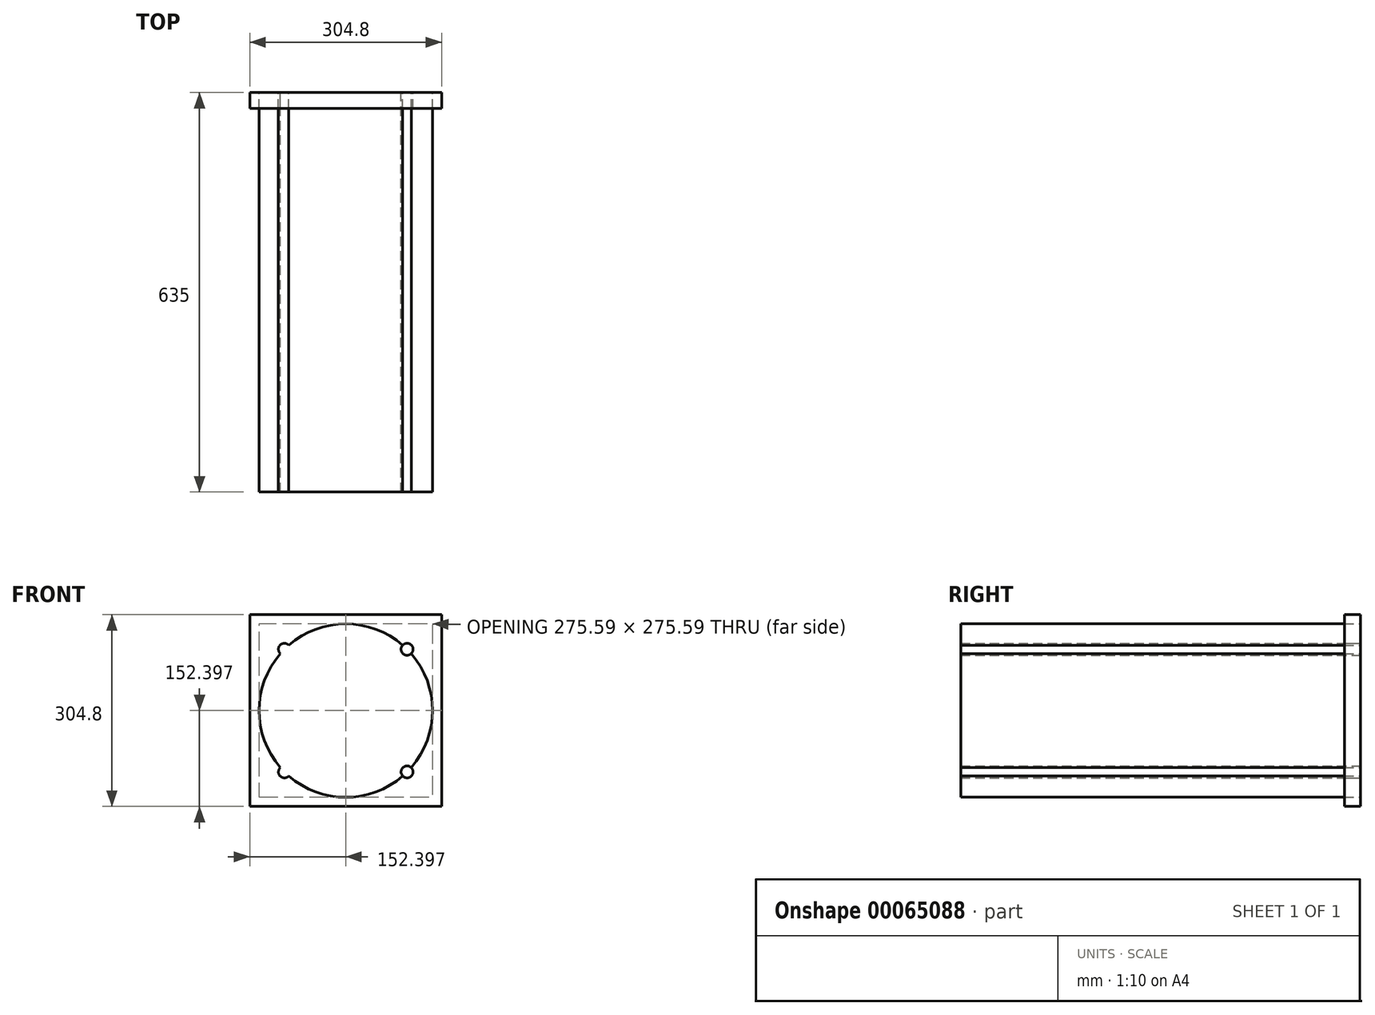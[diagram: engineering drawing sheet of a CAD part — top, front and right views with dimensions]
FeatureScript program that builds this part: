
annotation { "Feature Type Name" : "Feature", "Feature Type Description" : "" }
export const myFeature = defineFeature(function(context is Context, id is Id, definition is map)
    precondition{}
    {
        {
            var Q0;
            Q0=qCreatedBy(makeId("Front.planeOp"),FACE);
            var sketch = newSketch(context, id + "F0", { "sketchPlane" : qUnion([Q0])});
            skLineSegment(sketch, "E0.rect.bottom", {"start": v(140.94, 140.94) * mm, "end": v(-163.86, 140.94) * mm});
            skLineSegment(sketch, "E0.rect.top", {"start": v(140.94, -163.86) * mm, "end": v(-163.86, -163.86) * mm});
            skLineSegment(sketch, "E0.rect.left", {"start": v(140.94, 140.94) * mm, "end": v(140.94, -163.86) * mm});
            skLineSegment(sketch, "E0.rect.right", {"start": v(-163.86, 140.94) * mm, "end": v(-163.86, -163.86) * mm});
            skPoint(sketch, "E0.rect.middle", {"position": v(-11.46, -11.46) * mm});
            skCircle(sketch, "E1", {"center": v(-11.46, -11.46) * mm, "radius": 137.8 * mm});
            skCircle(sketch, "E2", {"center": v(-11.46, -11.46) * mm, "radius": 128.27 * mm, "construction": true});
            skLineSegment(sketch, "E3", {"start": v(-11.46, -11.46) * mm, "end": v(140.94, 140.94) * mm, "construction": true});
            skPoint(sketch, "E4", {"position": v(85.97, 85.97) * mm});
            skCircle(sketch, "E5", {"center": v(85.97, 85.97) * mm, "radius": 9.53 * mm});
            skLineSegment(sketch, "E6", {"start": v(-163.86, 140.94) * mm, "end": v(-11.46, -11.46) * mm, "construction": true});
            skCircle(sketch, "E7", {"center": v(-108.9, 85.97) * mm, "radius": 9.53 * mm});
            skLineSegment(sketch, "E8", {"start": v(-11.46, -11.46) * mm, "end": v(-163.86, -163.86) * mm, "construction": true});
            skLineSegment(sketch, "E9", {"start": v(-11.46, -11.46) * mm, "end": v(140.94, -163.86) * mm, "construction": true});
            skCircle(sketch, "E10", {"center": v(-108.9, -108.9) * mm, "radius": 9.53 * mm});
            skCircle(sketch, "E11", {"center": v(85.97, -108.9) * mm, "radius": 9.53 * mm});
            skSolve(sketch);
        }
        {
            var Q0;
            {var subQ0=sQuery(id+"F0.wireOp",EDGE,"E7");var subQ1=sQuery(id+"F0.wireOp",EDGE,"E1");var subQ2=makeQuery(id+"F0.imprint","INTERSECT",VERTEX,{"disambiguationData":[OD(0.0)],"derivedFrom":[subQ1,subQ0]});Q0=makeQuery(id+"F0.imprint","IMPRINT",FACE,{"disambiguationData":[TD([[makeQuery(id+"F0.imprint","IMPRINT",EDGE,{"disambiguationData":[TD([[subQ2,-1.0]])],"derivedFrom":subQ1}),1.0]])]});}
            var Q1;
            {var subQ0=sQuery(id+"F0.wireOp",EDGE,"E7");var subQ1=sQuery(id+"F0.wireOp",EDGE,"E1");var subQ2=makeQuery(id+"F0.imprint","INTERSECT",VERTEX,{"disambiguationData":[OD(0.0)],"derivedFrom":[subQ1,subQ0]});Q1=makeQuery(id+"F0.imprint","IMPRINT",FACE,{"disambiguationData":[TD([[makeQuery(id+"F0.imprint","IMPRINT",EDGE,{"disambiguationData":[TD([[subQ2,-1.0]])],"derivedFrom":subQ1}),-1.0]])]});}
            var Q2;
            {var subQ0=sQuery(id+"F0.wireOp",EDGE,"E5");var subQ1=sQuery(id+"F0.wireOp",EDGE,"E1");var subQ2=makeQuery(id+"F0.imprint","INTERSECT",VERTEX,{"disambiguationData":[OD(0.0)],"derivedFrom":[subQ1,subQ0]});Q2=makeQuery(id+"F0.imprint","IMPRINT",FACE,{"disambiguationData":[TD([[makeQuery(id+"F0.imprint","IMPRINT",EDGE,{"disambiguationData":[TD([[subQ2,1.0]])],"derivedFrom":subQ1}),-1.0]])]});}
            var Q3;
            {var subQ0=sQuery(id+"F0.wireOp",EDGE,"E5");var subQ1=sQuery(id+"F0.wireOp",EDGE,"E1");var subQ2=makeQuery(id+"F0.imprint","INTERSECT",VERTEX,{"disambiguationData":[OD(0.0)],"derivedFrom":[subQ1,subQ0]});Q3=makeQuery(id+"F0.imprint","IMPRINT",FACE,{"disambiguationData":[TD([[makeQuery(id+"F0.imprint","IMPRINT",EDGE,{"disambiguationData":[TD([[subQ2,1.0]])],"derivedFrom":subQ1}),1.0]])]});}
            var Q4;
            {var subQ0=sQuery(id+"F0.wireOp",EDGE,"E10");var subQ1=sQuery(id+"F0.wireOp",EDGE,"E1");var subQ2=makeQuery(id+"F0.imprint","INTERSECT",VERTEX,{"disambiguationData":[OD(0.0)],"derivedFrom":[subQ1,subQ0]});Q4=makeQuery(id+"F0.imprint","IMPRINT",FACE,{"disambiguationData":[TD([[makeQuery(id+"F0.imprint","IMPRINT",EDGE,{"disambiguationData":[TD([[subQ2,-1.0]])],"derivedFrom":subQ1}),-1.0]])]});}
            var Q5;
            {var subQ0=sQuery(id+"F0.wireOp",EDGE,"E10");var subQ1=sQuery(id+"F0.wireOp",EDGE,"E1");var subQ2=makeQuery(id+"F0.imprint","INTERSECT",VERTEX,{"disambiguationData":[OD(0.0)],"derivedFrom":[subQ1,subQ0]});Q5=makeQuery(id+"F0.imprint","IMPRINT",FACE,{"disambiguationData":[TD([[makeQuery(id+"F0.imprint","IMPRINT",EDGE,{"disambiguationData":[TD([[subQ2,-1.0]])],"derivedFrom":subQ1}),1.0]])]});}
            var Q6;
            {var subQ0=sQuery(id+"F0.wireOp",EDGE,"E11");var subQ1=sQuery(id+"F0.wireOp",EDGE,"E1");var subQ2=makeQuery(id+"F0.imprint","INTERSECT",VERTEX,{"disambiguationData":[OD(0.0)],"derivedFrom":[subQ1,subQ0]});Q6=makeQuery(id+"F0.imprint","IMPRINT",FACE,{"disambiguationData":[TD([[makeQuery(id+"F0.imprint","IMPRINT",EDGE,{"disambiguationData":[TD([[subQ2,-1.0]])],"derivedFrom":subQ1}),1.0]])]});}
            var Q7;
            {var subQ0=sQuery(id+"F0.wireOp",EDGE,"E11");var subQ1=sQuery(id+"F0.wireOp",EDGE,"E1");var subQ2=makeQuery(id+"F0.imprint","INTERSECT",VERTEX,{"disambiguationData":[OD(0.0)],"derivedFrom":[subQ1,subQ0]});Q7=makeQuery(id+"F0.imprint","IMPRINT",FACE,{"disambiguationData":[TD([[makeQuery(id+"F0.imprint","IMPRINT",EDGE,{"disambiguationData":[TD([[subQ2,-1.0]])],"derivedFrom":subQ1}),-1.0]])]});}
            extrude(context, id + "F1", {"entities" : qUnion([Q0, Q1, Q2, Q3, Q4, Q5, Q6, Q7]), "depth" : 635 * mm});
        }
        {
            var Q0;
            Q0 = qSketchRegion(id + "F0", true);
            extrude(context, id + "F2", {"entities" : qUnion([Q0]), "depth" : 25.4 * mm});
        }
    });
